# Revit family: QF_WELBILT-CONVOTHERM_CMX-PRO-ET-20-20-GS.240704053929
name_source: partatom
category: Specialty Equipment
units: mm (PartAtom-declared; Revit-internal decimal feet)

## family parameters
Always vertical = Yes
Cut with Voids When Loaded = No
OmniClass Number = 23.40.40.14
OmniClass Title = Food Service Equipment
Part Type = Normal
Room Calculation Point = No
Round Connector Dimension = Use Diameter
Shared = No
Work Plane-Based = No

## types (1)
- CMX-PRO-ET-20-20-GS-DD_230V/1Ph/50Hz
    Accessory = No
    Apparent Power = 1100 VA
    Cold Water Flow = 0.0 L/s
    Cold Water Size = 19 mm
    Cold Water Temperature Recommended = 0 °C
    Conn Conduit = No
    Cost = 0 $
    Cycle = 50 Hz
    Default Elevation = 0 mm  [stored 0 ft]
    Depth Actual = 1020 mm  [stored 3.34646 ft]
    Description = COMBI OVEN MAXX PRO EASYTOUCH 20 SHELVES GN 2/1 - DISAPPEARING DOOR - GAS INJECTION
    Electric power = 1100 W
    FL Amps = 4 A
    Gas Flow = 0.0 L/s
    Gas Size = 19 mm
    Gas Size Flexible = 0 mm
    Gas power kW = 62
    Height Actual = 1934 mm  [stored 6.34514 ft]
    Indirect Waste Size = 25 mm
    Length Actual = 1135 mm  [stored 3.72375 ft]
    Manufacturer = WELBILT-CONVOTHERM
    Max Overcurrent Protection = 0 A
    Min Ckt Ampacity = 0 A
    Model = CMX-PRO-ET-20-20-GS
    Nominal Gas power = 62000 W
    Number of Poles = 1
    Phase = 1
    URL = www.convotherm.com
    Volts = 230 V
    Weight = 331.00 kg

note: [stored X ft] marks values corroborated as IEEE doubles in the binary element streams (Revit-internal decimal feet)

## geometry (parser evidence)
native form markers: Sweep x3
no freeform markers — native parametric forms only
